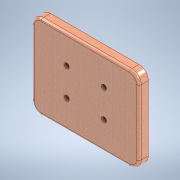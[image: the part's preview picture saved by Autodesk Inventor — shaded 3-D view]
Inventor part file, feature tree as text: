
AUTODESK INVENTOR PART (.ipt)
format: ipt  version: 2021.1 (Build 251245000, 245)  size: 188,928 bytes
history: native  units: in
note: dims shown in document units (in); Inventor stores cm internally (conversion verified against a paired STEP export)
features: extrude x3, fillet x1, sketch x1
ambient origin geometry x8: Origin, YZ Plane, XZ Plane, XY Plane, X Axis, Y Axis, Z Axis, Center Point
bodies: Solid1 (feature_tree)
feature tree (5):
  extrude  "Extrusion1"  Depth=18.0in
  fillet  "Fillet1"  Radius=2.0in
  extrude  "Extrusion2"  Depth=2.0in
  extrude  "Extrusion3"  Depth=2.0in TaperAngle=0.0deg
  sketch  "Sketch1"  dims[d0=23.0in d1=18.0in d2=2.0in d3=2.0in d4=2.0in d5=0.0in d6=0.5in d11=1.8in d12=1.1in d13=3.7041in d14=7.5in d15=1.8in d16=1.1in d17=3.0in d18=7.5in d19=0.0in d20=0.0in d21=1.1in d22=0.0in]
